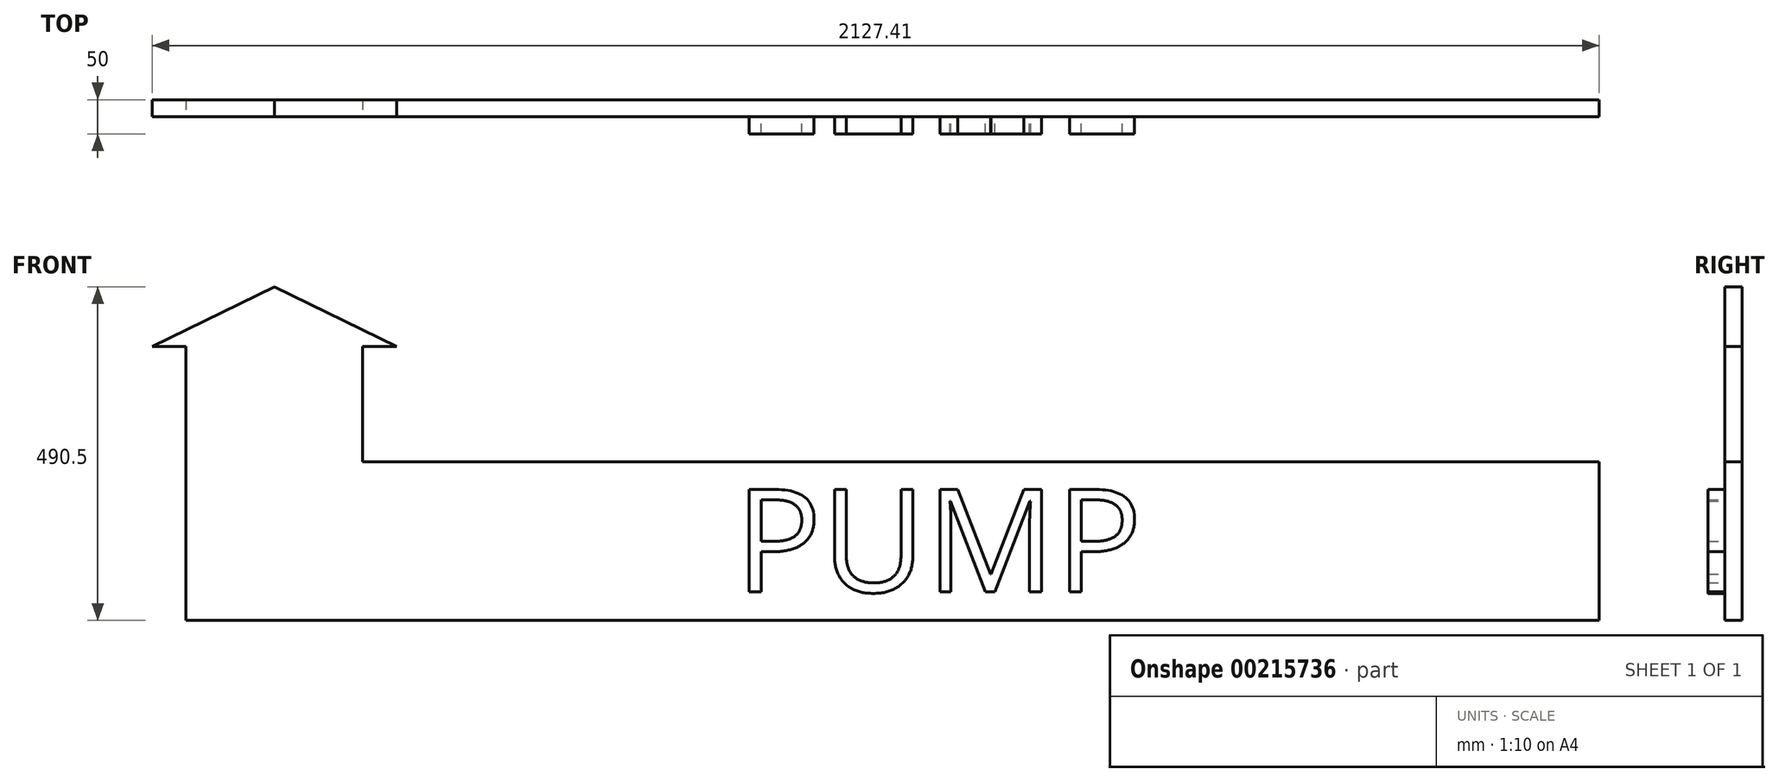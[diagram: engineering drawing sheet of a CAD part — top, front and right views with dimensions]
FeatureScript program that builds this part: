
annotation { "Feature Type Name" : "Feature", "Feature Type Description" : "" }
export const myFeature = defineFeature(function(context is Context, id is Id, definition is map)
    precondition{}
    {
        {
            var Q0;
            Q0=qCreatedBy(makeId("Front.planeOp"),FACE);
            var sketch = newSketch(context, id + "F0", { "sketchPlane" : qUnion([Q0])});
            skPoint(sketch, "E0.MirrorCS.end.orphan", {"position": v(0, 0) * mm});
            skLineSegment(sketch, "E1", {"start": v(-2046.82, 45.64) * mm, "end": v(-2046.82, 286.65) * mm});
            skPoint(sketch, "E2.MirrorCS.start.orphan", {"position": v(30.6, 279.02) * mm});
            skLineSegment(sketch, "E3", {"start": v(30.6, 279.02) * mm, "end": v(-1787.3, 279.02) * mm});
            skLineSegment(sketch, "E4", {"start": v(30.6, 279.02) * mm, "end": v(30.6, 45.64) * mm});
            skLineSegment(sketch, "E5", {"start": v(30.6, 45.64) * mm, "end": v(-2046.82, 45.64) * mm});
            skPoint(sketch, "E6", {"position": v(-2046.82, 551.1) * mm});
            skPoint(sketch, "E7.orphan", {"position": v(-1758.94, 551.1) * mm});
            skPoint(sketch, "E8.end.orphan", {"position": v(-1902.88, 551.1) * mm});
            skPoint(sketch, "E8.start.orphan", {"position": v(-2153.52, 279.02) * mm});
            skLineSegment(sketch, "E9", {"start": v(-2046.82, 286.65) * mm, "end": v(-2046.82, 448.46) * mm});
            skLineSegment(sketch, "E10", {"start": v(-2046.82, 448.46) * mm, "end": v(-2096.82, 448.46) * mm});
            skLineSegment(sketch, "E11", {"start": v(-1917.06, 536.14) * mm, "end": v(-1737.3, 448.46) * mm});
            skLineSegment(sketch, "E12", {"start": v(-1737.3, 448.46) * mm, "end": v(-1787.3, 448.46) * mm});
            skLineSegment(sketch, "E13", {"start": v(-1787.3, 448.46) * mm, "end": v(-1787.3, 279.02) * mm});
            skLineSegment(sketch, "E14", {"start": v(-1917.06, 536.14) * mm, "end": v(-2096.82, 448.46) * mm});
            skSolve(sketch);
        }
        {
            var Q0;
            Q0=qSketchRegion(id+"F0",true);
            extrude(context, id + "F1", {"entities" : qUnion([Q0]), "oppositeDirection" : true, "depth" : 25 * mm});
        }
        {
            var Q0;
            Q0=qCreatedBy(makeId("Front.planeOp"),FACE);
            var sketch = newSketch(context, id + "F2", { "sketchPlane" : qUnion([Q0])});
            skText(sketch, "E15", { "text": "PUMP", "fontName": "OpenSans-Regular.ttf"});
            const initialGuessF2  = {"E15": [-1.2398, 0.08748, 1, 0, 0.15191]};
            skSetInitialGuess(sketch, initialGuessF2);
            skSolve(sketch);
        }
        {
            var Q0;
            Q0=qSketchRegion(id+"F2",true);
            extrude(context, id + "F3", {"entities" : qUnion([Q0]), "operationType" : NewBodyOperationType.ADD, "flatOperationType" : FlatOperationType.REMOVE, "offsetDistance" : 25 * mm, "depth" : 25 * mm, "domain" : OperationDomain.MODEL});
        }
    });
